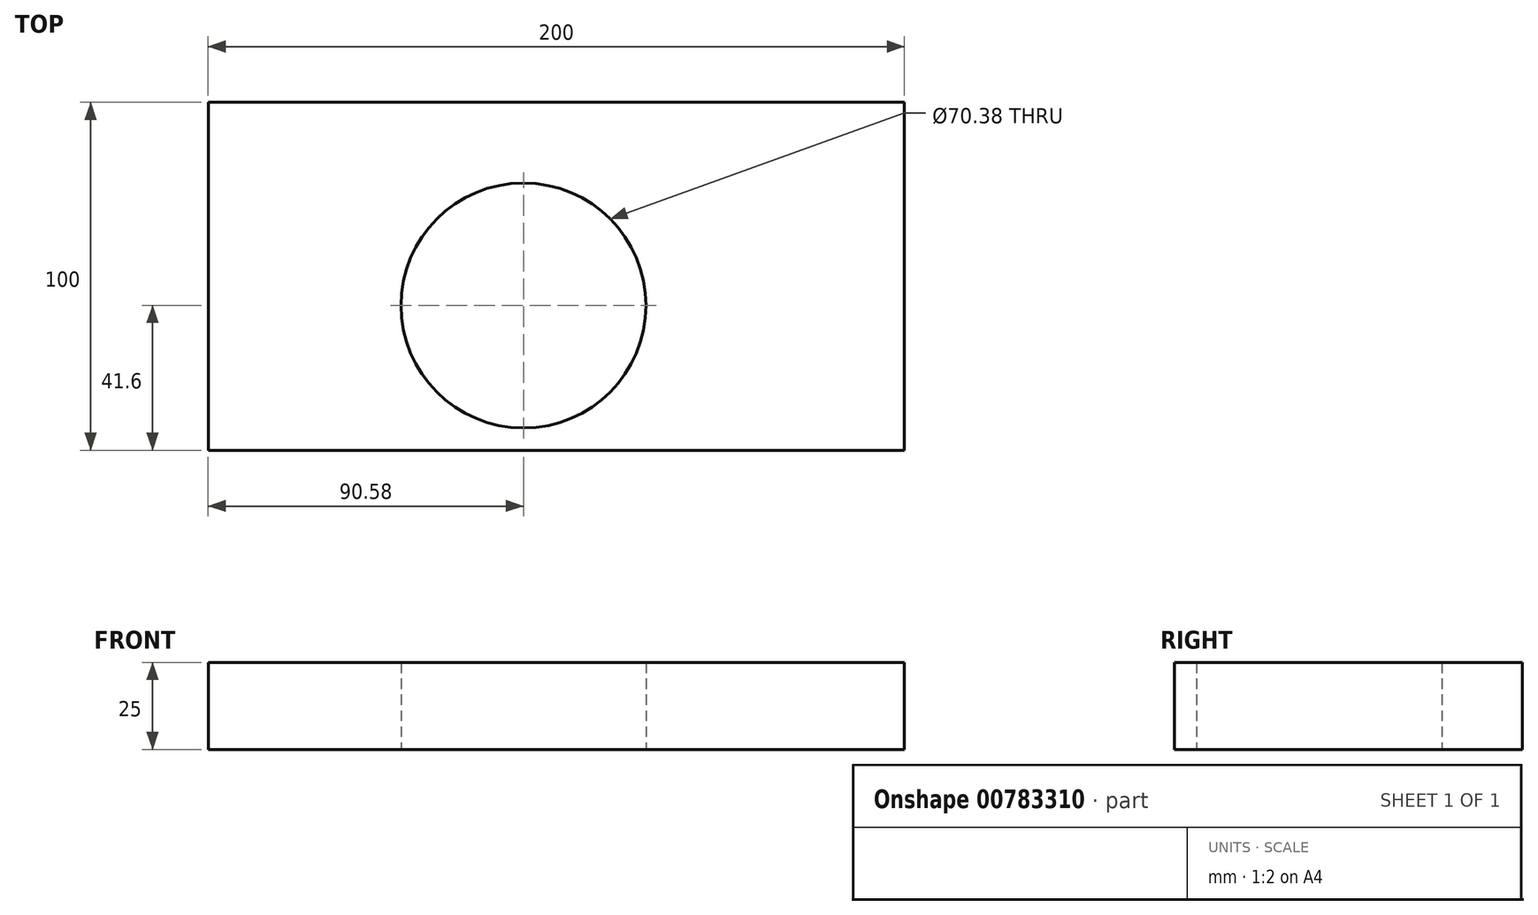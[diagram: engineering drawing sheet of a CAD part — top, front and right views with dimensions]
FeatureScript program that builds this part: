
annotation { "Feature Type Name" : "Feature", "Feature Type Description" : "" }
export const myFeature = defineFeature(function(context is Context, id is Id, definition is map)
    precondition{}
    {
        {
            var Q0;
            Q0=qCreatedBy(makeId("Top.planeOp"),FACE);
            var sketch = newSketch(context, id + "F0", { "sketchPlane" : qUnion([Q0])});
            skLineSegment(sketch, "E0.bottom", {"start": v(109.42, -41.6) * mm, "end": v(-90.58, -41.6) * mm});
            skLineSegment(sketch, "E0.top", {"start": v(109.42, 58.4) * mm, "end": v(-90.58, 58.4) * mm});
            skLineSegment(sketch, "E0.left", {"start": v(109.42, -41.6) * mm, "end": v(109.42, 58.4) * mm});
            skLineSegment(sketch, "E0.right", {"start": v(-90.58, -41.6) * mm, "end": v(-90.58, 58.4) * mm});
            skPoint(sketch, "E0.middle", {"position": v(9.42, 8.4) * mm});
            skCircle(sketch, "E1", {"center": v(0, 0) * mm, "radius": 35.2 * mm});
            skSolve(sketch);
        }
        {
            var Q0;
            Q0 = qSketchRegion(id + "F0", true);
            extrude(context, id + "F1", {"entities" : qUnion([Q0]), "depth" : 25 * mm, "offsetDistance" : 25 * mm});
        }
        {
            var Q0;
            Q0=makeQuery(id+"F1.opExtrude","CAP_FACE",FACE,{"disambiguationData":[OSD([sQuery(id+"F0.wireOp",EDGE,"E0.bottom"),sQuery(id+"F0.wireOp",EDGE,"E0.top"),sQuery(id+"F0.wireOp",EDGE,"E0.left"),sQuery(id+"F0.wireOp",EDGE,"E0.right"),sQuery(id+"F0.wireOp",EDGE,"E1")])],"isStart":false});
            var sketch = newSketch(context, id + "F2", { "sketchPlane" : qUnion([Q0])});
            skLineSegment(sketch, "E2.bottom", {"start": v(-72.43, 58.4) * mm, "end": v(-60.93, 58.4) * mm});
            skLineSegment(sketch, "E2.top", {"start": v(-72.43, -41.6) * mm, "end": v(-60.93, -41.6) * mm});
            skLineSegment(sketch, "E2.left", {"start": v(-72.43, 58.4) * mm, "end": v(-72.43, -41.6) * mm});
            skLineSegment(sketch, "E2.right", {"start": v(-60.93, 58.4) * mm, "end": v(-60.93, -41.6) * mm});
            skSolve(sketch);
        }
        {
            var Q0;
            Q0=makeQuery(id+"F2.imprint","IMPRINT",FACE,{"disambiguationData":[TD([[makeQuery(id+"F2.imprint","IMPRINT",EDGE,{"derivedFrom":sQuery(id+"F2.wireOp",EDGE,"E2.bottom")}),1.0]])]});
            var sketch = newSketch(context, id + "F3", { "sketchPlane" : qUnion([Q0])});
            skSolve(sketch);
        }
        {
            var Q0;
            Q0=makeQuery(id+"F3.imprint","IMPRINT",FACE,{"disambiguationData":[TD([[makeQuery(id+"F3.imprint","IMPRINT",EDGE,{"derivedFrom":makeQuery(id+"F2.imprint","IMPRINT",EDGE,{"derivedFrom":sQuery(id+"F2.wireOp",EDGE,"E2.bottom")})}),1.0]])]});
            extrude(context, id + "F4", {"entities" : qUnion([Q0]), "operationType" : NewBodyOperationType.ADD, "oppositeDirection" : true, "depth" : 10 * mm, "offsetDistance" : 25 * mm});
        }
        {
            var Q0;
            Q0=makeQuery(id+"F2.imprint","IMPRINT",FACE,{"disambiguationData":[TD([[makeQuery(id+"F2.imprint","IMPRINT",EDGE,{"derivedFrom":sQuery(id+"F2.wireOp",EDGE,"E2.bottom")}),1.0]])]});
            var sketch = newSketch(context, id + "F5", { "sketchPlane" : qUnion([Q0])});
            skSolve(sketch);
        }
        {
            var Q0;
            Q0=makeQuery(id+"F5.imprint","IMPRINT",FACE,{"disambiguationData":[TD([[makeQuery(id+"F5.imprint","IMPRINT",EDGE,{"derivedFrom":makeQuery(id+"F2.imprint","IMPRINT",EDGE,{"derivedFrom":sQuery(id+"F2.wireOp",EDGE,"E2.bottom")})}),1.0]])]});
            extrude(context, id + "F6", {"entities" : qUnion([Q0]), "operationType" : NewBodyOperationType.ADD, "oppositeDirection" : true, "depth" : 10 * mm, "offsetDistance" : 25 * mm});
        }
    });
